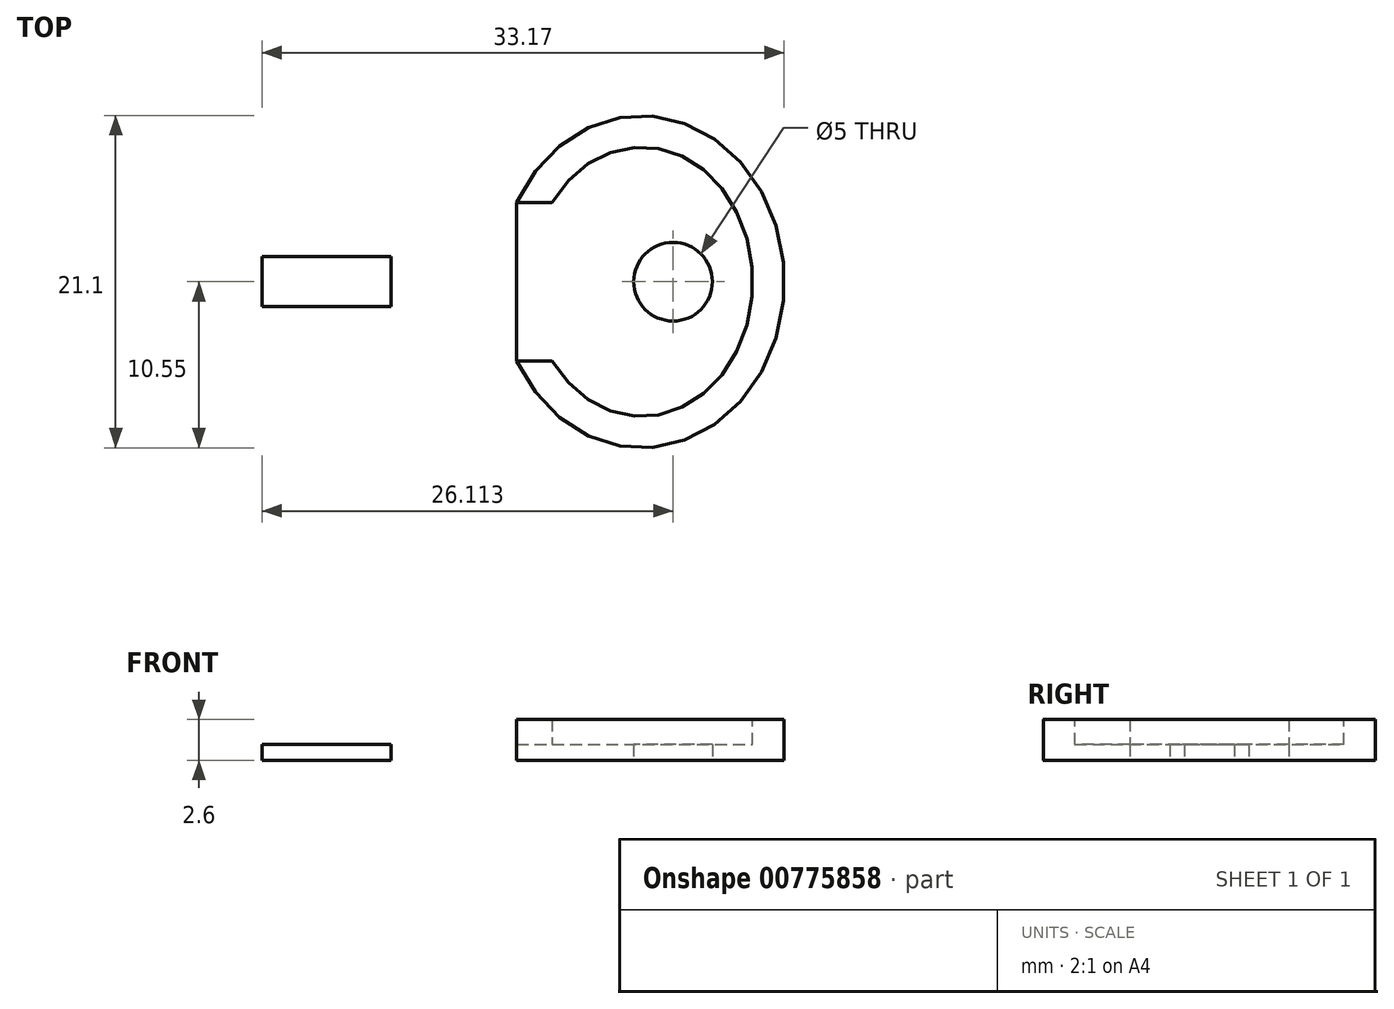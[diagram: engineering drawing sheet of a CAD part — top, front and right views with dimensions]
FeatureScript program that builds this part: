
annotation { "Feature Type Name" : "Feature", "Feature Type Description" : "" }
export const myFeature = defineFeature(function(context is Context, id is Id, definition is map)
    precondition{}
    {
        {
            var Q0;
            Q0=qCreatedBy(makeId("Top.planeOp"),FACE);
            var sketch = newSketch(context, id + "F0", { "sketchPlane" : qUnion([Q0])});
            skEllipse(sketch, "E0", {"center": v(0, 0) * mm, "majorRadius": 8.55 * mm, "minorRadius": 7.05 * mm, "majorAxis": v(0, 1)});
            skEllipticalArc(sketch, "E1", {});
            skLineSegment(sketch, "E2", {"start": v(0, 10.55) * mm, "end": v(0, 8.55) * mm, "construction": true});
            skLineSegment(sketch, "E3", {"start": v(-7.05, 0) * mm, "end": v(-7.95, 0) * mm, "construction": true});
            skLineSegment(sketch, "E4", {"start": v(7.05, 0) * mm, "end": v(0, 0) * mm});
            skLineSegment(sketch, "E5", {"start": v(-7.95, 0) * mm, "end": v(-7.95, 5.04) * mm});
            skLineSegment(sketch, "E6.MirrorCS", {"start": v(-7.95, 0) * mm, "end": v(-7.95, -5.04) * mm});
            skPoint(sketch, "E7.orphan", {"position": v(-7.95, 8.08) * mm});
            skPoint(sketch, "E8.orphan", {"position": v(-7.95, -8.08) * mm});
            skPoint(sketch, "E9.orphan", {"position": v(-9.05, 0) * mm});
            skLineSegment(sketch, "E10.trimOffspring", {"start": v(-7.05, 0) * mm, "end": v(-7.95, 0) * mm});
            skLineSegment(sketch, "E11", {"start": v(7.05, 0) * mm, "end": v(0.05, 0) * mm, "construction": true});
            skLineSegment(sketch, "E12", {"start": v(7.05, 0) * mm, "end": v(4.05, 0) * mm, "construction": true});
            skCircle(sketch, "E13", {"center": v(2, 0) * mm, "radius": 2.5 * mm});
            skLineSegment(sketch, "E14", {"start": v(-7.95, 5.04) * mm, "end": v(-5.7, 5.04) * mm});
            skLineSegment(sketch, "E15.MirrorCS", {"start": v(-7.95, -5.04) * mm, "end": v(-5.7, -5.04) * mm});
            skLineSegment(sketch, "E16.bottom", {"start": v(-24.12, -1.58) * mm, "end": v(-15.92, -1.58) * mm});
            skLineSegment(sketch, "E16.top", {"start": v(-24.12, 1.58) * mm, "end": v(-15.92, 1.58) * mm});
            skLineSegment(sketch, "E16.left", {"start": v(-24.12, -1.58) * mm, "end": v(-24.12, 1.58) * mm});
            skLineSegment(sketch, "E16.right", {"start": v(-15.92, -1.58) * mm, "end": v(-15.92, 1.58) * mm});
            skPoint(sketch, "E16.middle", {"position": v(-20.02, 0) * mm});
            skLineSegment(sketch, "E17", {"start": v(-7.95, 0) * mm, "end": v(-29.95, 0) * mm, "construction": true});
            const initialGuessF0  = {"E1": [0, 0, 0, 1, 0.01055, 0.00905, 2.068977632207929, 1.0726150213818642]};
            skSetInitialGuess(sketch, initialGuessF0);
            skSolve(sketch);
        }
        {
            var Q0;
            Q0=makeQuery(id+"F0.imprint","IMPRINT",FACE,{"disambiguationData":[TD([[makeQuery(id+"F0.imprint","IMPRINT",EDGE,{"derivedFrom":sQuery(id+"F0.wireOp",EDGE,"E1")}),1.0]])]});
            extrude(context, id + "F1", {"entities" : qUnion([Q0]), "depth" : 2.6 * mm, "offsetDistance" : 25 * mm});
        }
        {
            var Q0;
            Q0=makeQuery(id+"F0.imprint","IMPRINT",FACE,{"disambiguationData":[TD([[makeQuery(id+"F0.imprint","IMPRINT",EDGE,{"derivedFrom":sQuery(id+"F0.wireOp",EDGE,"E13")}),-1.0]])]});
            var Q1;
            Q1=makeQuery(id+"F0.imprint","IMPRINT",FACE,{"disambiguationData":[TD([[makeQuery(id+"F0.imprint","IMPRINT",EDGE,{"derivedFrom":sQuery(id+"F0.wireOp",EDGE,"E6.MirrorCS")}),1.0]])]});
            var Q2;
            Q2=makeQuery(id+"F0.imprint","IMPRINT",FACE,{"disambiguationData":[TD([[makeQuery(id+"F0.imprint","IMPRINT",EDGE,{"derivedFrom":sQuery(id+"F0.wireOp",EDGE,"E5")}),-1.0]])]});
            var Q3;
            Q3=makeQuery(id+"F0.imprint","IMPRINT",FACE,{"disambiguationData":[TD([[makeQuery(id+"F0.imprint","IMPRINT",EDGE,{"derivedFrom":sQuery(id+"F0.wireOp",EDGE,"E16.bottom")}),1.0]])]});
            extrude(context, id + "F2", {"entities" : qUnion([Q0, Q1, Q2, Q3]), "operationType" : NewBodyOperationType.ADD, "depth" : 1 * mm, "offsetDistance" : 25 * mm});
        }
    });
